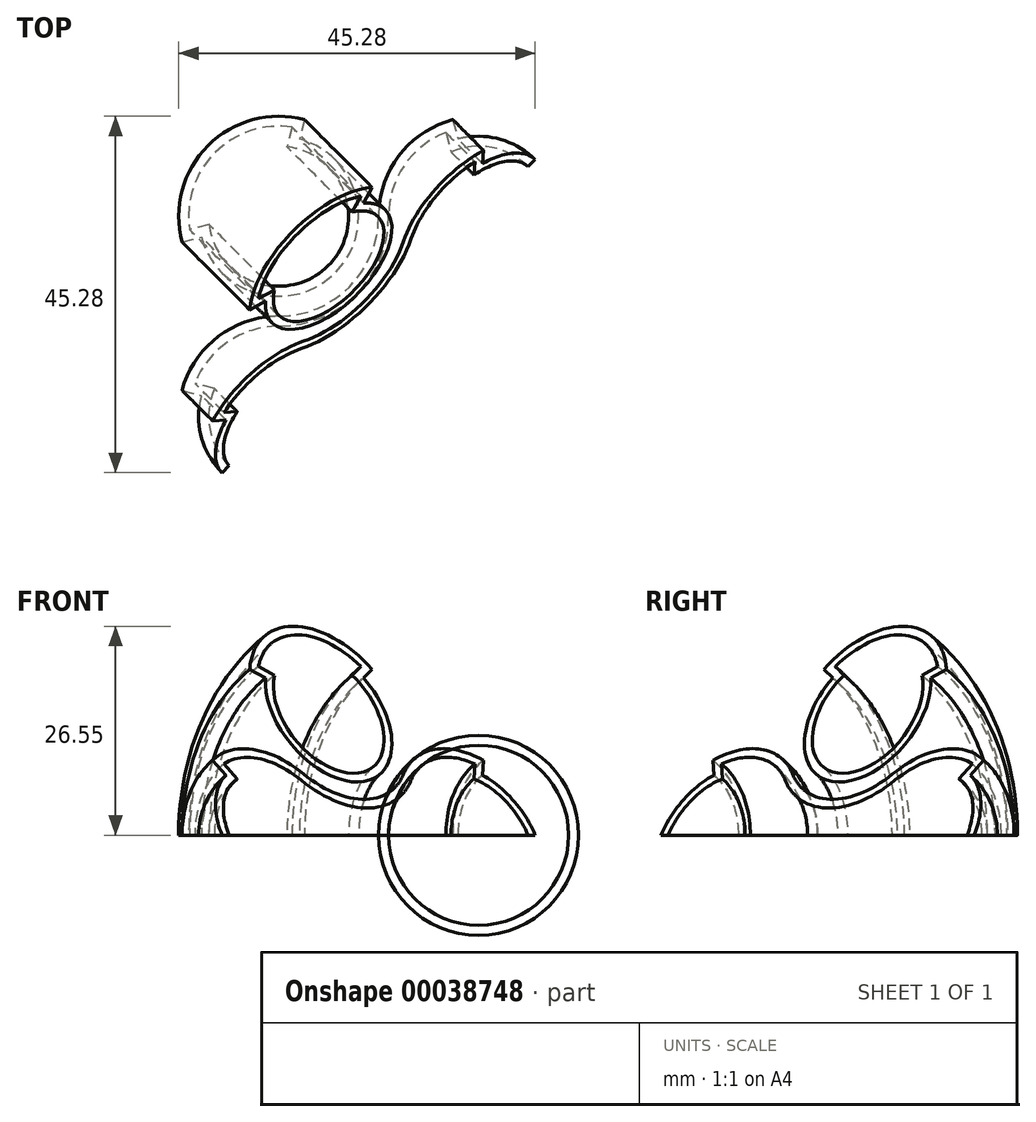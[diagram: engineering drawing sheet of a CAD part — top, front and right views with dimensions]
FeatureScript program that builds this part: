
annotation { "Feature Type Name" : "Feature", "Feature Type Description" : "" }
export const myFeature = defineFeature(function(context is Context, id is Id, definition is map)
    precondition{}
    {
        {
            var Q0;
            Q0=qCreatedBy(makeId("Top.planeOp"),FACE);
            var sketch = newSketch(context, id + "F0", { "sketchPlane" : qUnion([Q0])});
            skCircle(sketch, "E0.0", {"center": v(0, 0) * mm, "radius": 10.16 * mm});
            skLineSegment(sketch, "E1", {"start": v(34.38, 34.38) * mm, "end": v(-8.98, -8.98) * mm});
            skLineSegment(sketch, "E2", {"start": v(-12.27, 3.29) * mm, "end": v(-9.81, 2.63) * mm});
            skLineSegment(sketch, "E3", {"start": v(3.29, -12.27) * mm, "end": v(2.63, -9.81) * mm});
            skArc(sketch, "E4", {"start": v(-12.27, 3.29) * mm, "mid": v(-8.98, -8.98) * mm, "end": v(3.29, -12.27) * mm, "construction": true});
            skArc(sketch, "E5", {"start": v(3.29, -12.27) * mm, "mid": v(8.98, 8.98) * mm, "end": v(-12.27, 3.29) * mm});
            skLineSegment(sketch, "E6", {"start": v(-12.27, 3.29) * mm, "end": v(-24.53, 6.57) * mm, "construction": true});
            skLineSegment(sketch, "E7", {"start": v(-24.53, 6.57) * mm, "end": v(6.57, -24.53) * mm, "construction": true});
            skLineSegment(sketch, "E8", {"start": v(6.57, -24.53) * mm, "end": v(3.29, -12.27) * mm, "construction": true});
            skLineSegment(sketch, "E9", {"start": v(0, 12.7) * mm, "end": v(12.7, 12.7) * mm, "construction": true});
            skLineSegment(sketch, "E10", {"start": v(12.7, 12.7) * mm, "end": v(12.7, 0) * mm, "construction": true});
            skArc(sketch, "E11.1.0", {"start": v(37.67, 3.29) * mm, "mid": v(16.42, 8.98) * mm, "end": v(22.11, -12.27) * mm});
            skLineSegment(sketch, "E11.1.1", {"start": v(22.11, -12.27) * mm, "end": v(22.77, -9.81) * mm});
            skCircle(sketch, "E11.1.2", {"center": v(25.4, 0) * mm, "radius": 10.16 * mm});
            skLineSegment(sketch, "E11.1.3", {"start": v(37.67, 3.29) * mm, "end": v(35.21, 2.63) * mm});
            skArc(sketch, "E11.1.4", {"start": v(22.11, -12.27) * mm, "mid": v(34.38, -8.98) * mm, "end": v(37.67, 3.29) * mm});
            skArc(sketch, "E11.2.0", {"start": v(22.11, 37.67) * mm, "mid": v(16.42, 16.42) * mm, "end": v(37.67, 22.11) * mm});
            skLineSegment(sketch, "E11.2.1", {"start": v(37.67, 22.11) * mm, "end": v(35.21, 22.77) * mm});
            skCircle(sketch, "E11.2.2", {"center": v(25.4, 25.4) * mm, "radius": 10.16 * mm});
            skLineSegment(sketch, "E11.2.3", {"start": v(22.11, 37.67) * mm, "end": v(22.77, 35.21) * mm});
            skArc(sketch, "E11.2.4", {"start": v(37.67, 22.11) * mm, "mid": v(34.38, 34.38) * mm, "end": v(22.11, 37.67) * mm, "construction": true});
            skArc(sketch, "E11.3.0", {"start": v(-12.27, 22.11) * mm, "mid": v(8.98, 16.42) * mm, "end": v(3.29, 37.67) * mm});
            skLineSegment(sketch, "E11.3.1", {"start": v(3.29, 37.67) * mm, "end": v(2.63, 35.21) * mm});
            skCircle(sketch, "E11.3.2", {"center": v(0, 25.4) * mm, "radius": 10.16 * mm});
            skLineSegment(sketch, "E11.3.3", {"start": v(-12.27, 22.11) * mm, "end": v(-9.81, 22.77) * mm});
            skArc(sketch, "E11.3.4", {"start": v(3.29, 37.67) * mm, "mid": v(-8.98, 34.38) * mm, "end": v(-12.27, 22.11) * mm});
            skPoint(sketch, "E11.center", {"position": v(12.7, 12.7) * mm});
            skCircle(sketch, "E12", {"center": v(0, 25.4) * mm, "radius": 17.96 * mm, "construction": true});
            skLineSegment(sketch, "E13", {"start": v(12.7, 12.7) * mm, "end": v(-12.7, 38.1) * mm, "construction": true});
            skLineSegment(sketch, "E14", {"start": v(25.4, 25.4) * mm, "end": v(0, 50.8) * mm, "construction": true});
            skLineSegment(sketch, "E15", {"start": v(-12.7, 38.1) * mm, "end": v(0, 50.8) * mm, "construction": true});
            skSolve(sketch);
        }
        {
            var Q0;
            {var subQ3=sQuery(id+"F0.wireOp",EDGE,"E2");Q0=makeQuery(id+"F0.imprint","IMPRINT",FACE,{"disambiguationData":[TD([[makeQuery(id+"F0.imprint","IMPRINT",EDGE,{"derivedFrom":subQ3}),1.0]])]});}
            var Q1;
            {var subQ1=sQuery(id+"F0.wireOp",EDGE,"E0.0");var subQ4=makeQuery(id+"F0.imprint","INTERSECT",VERTEX,{"derivedFrom":[subQ1,sQuery(id+"F0.wireOp",EDGE,"E2")]});Q1=makeQuery(id+"F0.imprint","IMPRINT",FACE,{"disambiguationData":[TD([[makeQuery(id+"F0.imprint","IMPRINT",EDGE,{"disambiguationData":[TD([[subQ4,1.0]])],"derivedFrom":subQ1}),1.0]])]});}
            var Q2;
            {var subQ0=sQuery(id+"F0.wireOp",EDGE,"E11.2.0");var subQ1=sQuery(id+"F0.wireOp",EDGE,"E1");var subQ2=makeQuery(id+"F0.imprint","INTERSECT",VERTEX,{"derivedFrom":[subQ1,subQ0]});Q2=makeQuery(id+"F0.imprint","IMPRINT",FACE,{"disambiguationData":[TD([[makeQuery(id+"F0.imprint","IMPRINT",EDGE,{"disambiguationData":[TD([[subQ2,-1.0]])],"derivedFrom":subQ1}),-1.0]])]});}
            var Q3;
            {var subQ0=sQuery(id+"F0.wireOp",EDGE,"E11.2.2");var subQ1=sQuery(id+"F0.wireOp",EDGE,"E1");var subQ4=makeQuery(id+"F0.imprint","INTERSECT",VERTEX,{"disambiguationData":[OD(0.0)],"derivedFrom":[subQ1,subQ0]});Q3=makeQuery(id+"F0.imprint","IMPRINT",FACE,{"disambiguationData":[TD([[makeQuery(id+"F0.imprint","IMPRINT",EDGE,{"disambiguationData":[TD([[subQ4,-1.0]])],"derivedFrom":subQ1}),-1.0]])]});}
            var Q4;
            {var subQ0=sQuery(id+"F0.wireOp",EDGE,"E11.2.3");Q4=makeQuery(id+"F0.imprint","IMPRINT",FACE,{"disambiguationData":[TD([[makeQuery(id+"F0.imprint","IMPRINT",EDGE,{"derivedFrom":subQ0}),-1.0]])]});}
            var Q5;
            {var subQ0=sQuery(id+"F0.wireOp",EDGE,"E11.3.2");var subQ2=makeQuery(id+"F0.imprint","INTERSECT",VERTEX,{"derivedFrom":[sQuery(id+"F0.wireOp",EDGE,"E11.3.1"),subQ0]});Q5=makeQuery(id+"F0.imprint","IMPRINT",FACE,{"disambiguationData":[TD([[makeQuery(id+"F0.imprint","IMPRINT",EDGE,{"disambiguationData":[TD([[subQ2,-1.0]])],"derivedFrom":subQ0}),1.0]])]});}
            var Q6;
            {var subQ2=sQuery(id+"F0.wireOp",EDGE,"E11.3.1");Q6=makeQuery(id+"F0.imprint","IMPRINT",FACE,{"disambiguationData":[TD([[makeQuery(id+"F0.imprint","IMPRINT",EDGE,{"derivedFrom":subQ2}),-1.0]])]});}
            var Q7;
            Q7=sQuery(id+"F0.wireOp",EDGE,"E1");
            revolve(context, id + "F1", {"surfaceOperationType" : NewSurfaceOperationType.NEW, "entities" : qUnion([Q0, Q1, Q2, Q3, Q4, Q5, Q6]), "axis" : qUnion([Q7]), "revolveType" : RevolveType.ONE_DIRECTION, "oppositeDirection" : true, "angle" : 60 * degree});
        }
        {
            var Q0;
            Q0=makeQuery(id+"F1.opRevolve","CAP_FACE",FACE,{"disambiguationData":[OSD([sQuery(id+"F0.wireOp",EDGE,"E0.0"),sQuery(id+"F0.wireOp",EDGE,"E1"),sQuery(id+"F0.wireOp",EDGE,"E2"),sQuery(id+"F0.wireOp",EDGE,"E5"),sQuery(id+"F0.wireOp",EDGE,"E11.2.0"),sQuery(id+"F0.wireOp",EDGE,"E11.2.2"),sQuery(id+"F0.wireOp",EDGE,"E11.2.3"),sQuery(id+"F0.wireOp",EDGE,"E11.3.0")])],"isStart":true});
            var Q1;
            Q1=makeQuery(id+"F1.opRevolve","CAP_FACE",FACE,{"disambiguationData":[OSD([sQuery(id+"F0.wireOp",EDGE,"E0.0"),sQuery(id+"F0.wireOp",EDGE,"E1"),sQuery(id+"F0.wireOp",EDGE,"E2"),sQuery(id+"F0.wireOp",EDGE,"E5"),sQuery(id+"F0.wireOp",EDGE,"E11.2.0"),sQuery(id+"F0.wireOp",EDGE,"E11.2.2"),sQuery(id+"F0.wireOp",EDGE,"E11.2.3"),sQuery(id+"F0.wireOp",EDGE,"E11.3.0")])],"isStart":false});
            var Q2;
            Q2=makeQuery(id+"F1.opRevolve","CAP_FACE",FACE,{"disambiguationData":[OSD([sQuery(id+"F0.wireOp",EDGE,"E11.3.1"),sQuery(id+"F0.wireOp",EDGE,"E11.3.2"),sQuery(id+"F0.wireOp",EDGE,"E11.3.3"),sQuery(id+"F0.wireOp",EDGE,"E11.3.4")])],"isStart":true});
            var Q3;
            Q3=makeQuery(id+"F1.opRevolve","CAP_FACE",FACE,{"disambiguationData":[OSD([sQuery(id+"F0.wireOp",EDGE,"E11.3.1"),sQuery(id+"F0.wireOp",EDGE,"E11.3.2"),sQuery(id+"F0.wireOp",EDGE,"E11.3.3"),sQuery(id+"F0.wireOp",EDGE,"E11.3.4")])],"isStart":false});
            shell(context, id + "F2", {"entities" : qUnion([Q0, Q1, Q2, Q3]), "thickness" : 1.27 * mm});
        }
    });
